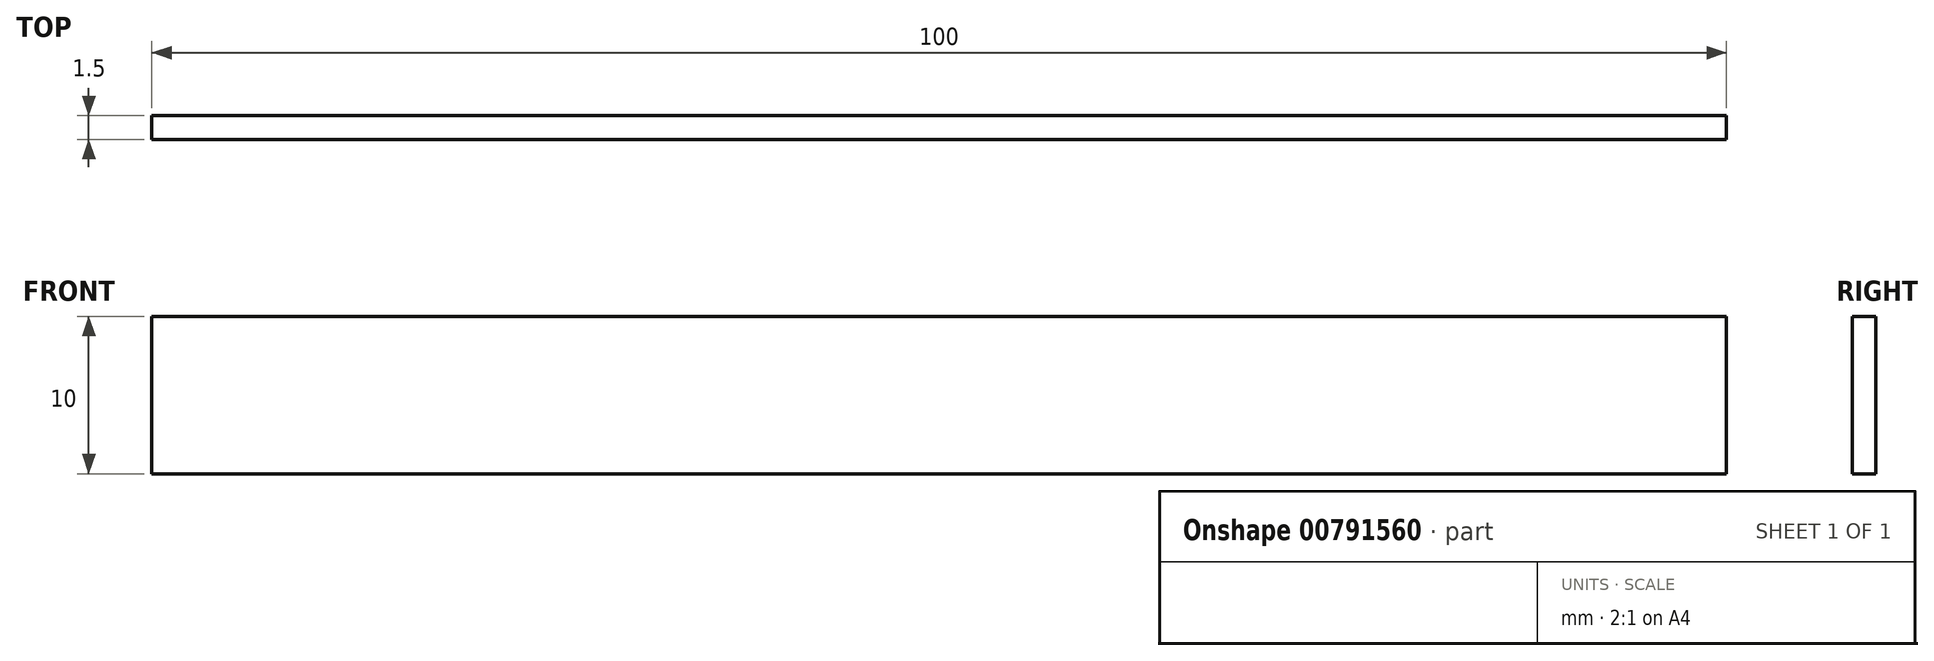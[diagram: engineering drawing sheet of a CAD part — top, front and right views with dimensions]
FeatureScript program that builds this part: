
annotation { "Feature Type Name" : "Feature", "Feature Type Description" : "" }
export const myFeature = defineFeature(function(context is Context, id is Id, definition is map)
    precondition{}
    {
        {
            var Q0;
            Q0=qCreatedBy(makeId("Front.planeOp"),FACE);
            var sketch = newSketch(context, id + "F0", { "sketchPlane" : qUnion([Q0])});
            skLineSegment(sketch, "E0.bottom", {"start": v(-46.44, 29.54) * mm, "end": v(53.56, 29.54) * mm});
            skLineSegment(sketch, "E0.top", {"start": v(-46.44, 19.54) * mm, "end": v(53.56, 19.54) * mm});
            skLineSegment(sketch, "E0.left", {"start": v(-46.44, 29.54) * mm, "end": v(-46.44, 19.54) * mm});
            skLineSegment(sketch, "E0.right", {"start": v(53.56, 29.54) * mm, "end": v(53.56, 19.54) * mm});
            skSolve(sketch);
        }
        {
            var Q0;
            Q0=makeQuery(id+"F0.imprint","IMPRINT",FACE,{"disambiguationData":[TD([[makeQuery(id+"F0.imprint","IMPRINT",EDGE,{"derivedFrom":sQuery(id+"F0.wireOp",EDGE,"E0.bottom")}),-1.0]])]});
            extrude(context, id + "F1", {"entities" : qUnion([Q0]), "depth" : 1.5 * mm, "offsetDistance" : 25 * mm});
        }
    });
